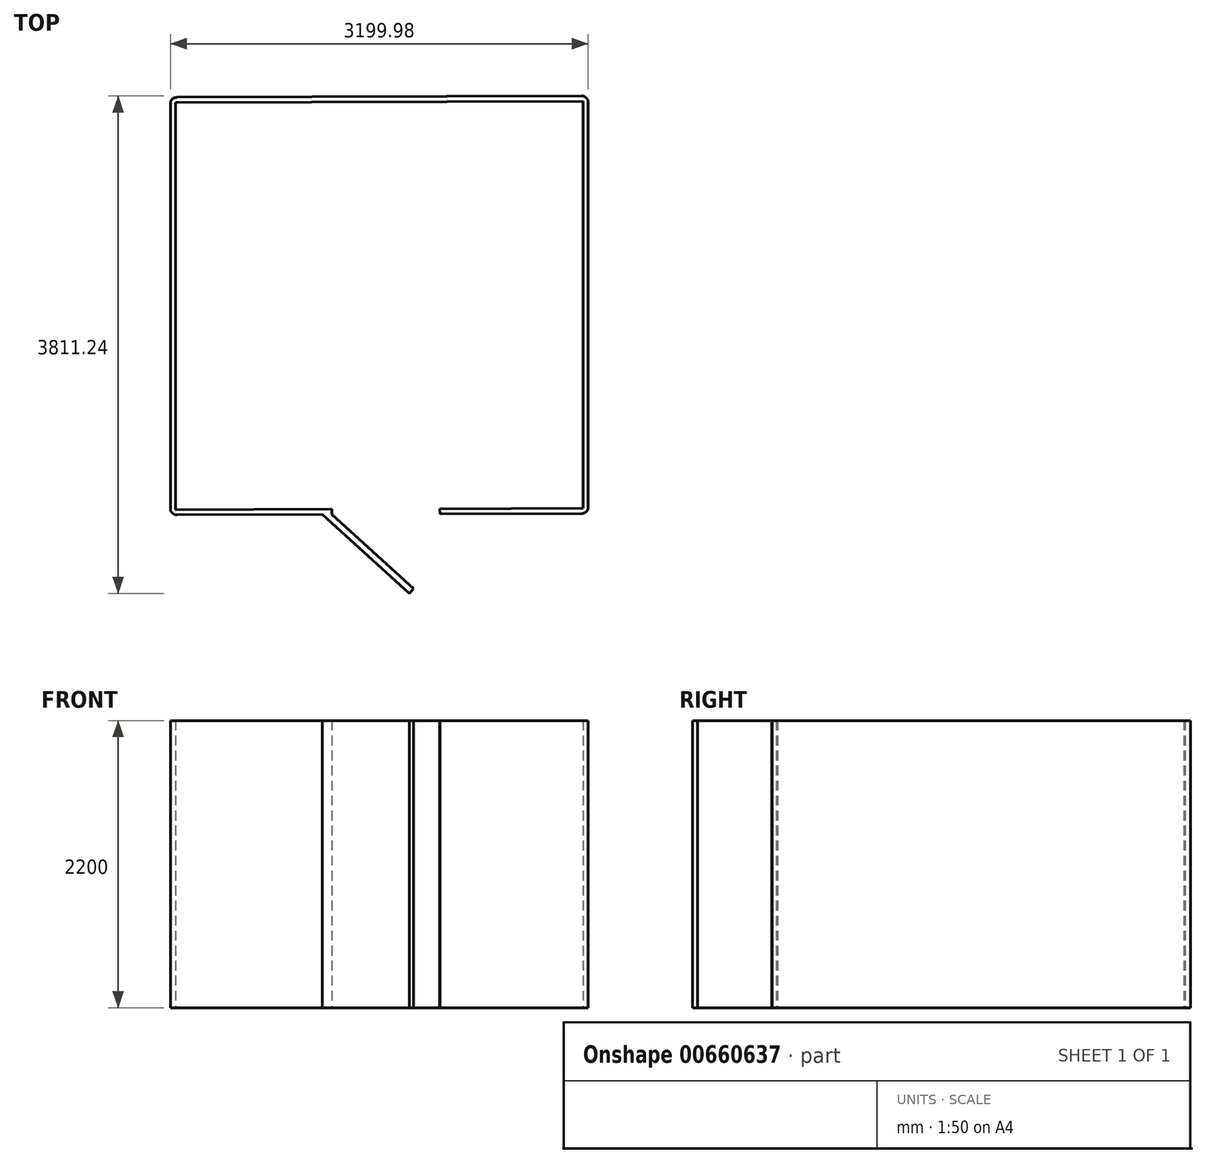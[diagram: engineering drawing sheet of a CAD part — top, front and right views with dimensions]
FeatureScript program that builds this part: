
annotation { "Feature Type Name" : "Feature", "Feature Type Description" : "" }
export const myFeature = defineFeature(function(context is Context, id is Id, definition is map)
    precondition{}
    {
        {
            var Q0;
            Q0=qCreatedBy(makeId("Top.planeOp"),FACE);
            var sketch = newSketch(context, id + "F0", { "sketchPlane" : qUnion([Q0])});
            skLineSegment(sketch, "E0", {"start": v(-163.84, 2276.46) * mm, "end": v(-163.84, -823.54) * mm});
            skLineSegment(sketch, "E1", {"start": v(-113.68, -873.54) * mm, "end": v(998.4, -869.87) * mm});
            skLineSegment(sketch, "E2", {"start": v(3036.14, -813.3) * mm, "end": v(3036.14, 2286.7) * mm});
            skLineSegment(sketch, "E3", {"start": v(2985.98, 2336.7) * mm, "end": v(-114, 2326.46) * mm});
            skLineSegment(sketch, "E4.0", {"start": v(-123.84, 2286.42) * mm, "end": v(-123.84, -833.58) * mm});
            skLineSegment(sketch, "E4.1", {"start": v(2996.14, 2296.74) * mm, "end": v(-123.84, 2286.42) * mm});
            skLineSegment(sketch, "E4.2", {"start": v(2996.14, -823.26) * mm, "end": v(2996.14, 2296.74) * mm});
            skLineSegment(sketch, "E4.3", {"start": v(-123.84, -833.58) * mm, "end": v(1072.4, -829.62) * mm});
            skPoint(sketch, "E5.visualSharp", {"position": v(-163.84, 2326.3) * mm});
            skArc(sketch, "E5.filletArc", {"start": v(-114, 2326.46) * mm, "mid": v(-149.25, 2311.75) * mm, "end": v(-163.84, 2276.46) * mm});
            skPoint(sketch, "E6.visualSharp", {"position": v(-163.84, -873.7) * mm});
            skArc(sketch, "E6.filletArc", {"start": v(-163.84, -823.54) * mm, "mid": v(-149.14, -858.96) * mm, "end": v(-113.68, -873.54) * mm});
            skPoint(sketch, "E7.visualSharp", {"position": v(3036.14, -863.13) * mm});
            skArc(sketch, "E7.filletArc", {"start": v(2986.3, -863.3) * mm, "mid": v(3021.56, -848.6) * mm, "end": v(3036.14, -813.3) * mm});
            skPoint(sketch, "E8.visualSharp", {"position": v(3036.14, 2336.87) * mm});
            skArc(sketch, "E8.filletArc", {"start": v(3036.14, 2286.7) * mm, "mid": v(3021.44, 2322.12) * mm, "end": v(2985.98, 2336.7) * mm});
            skLineSegment(sketch, "E9", {"start": v(998.4, -869.87) * mm, "end": v(1665, -1474.54) * mm});
            skLineSegment(sketch, "E10", {"start": v(1665, -1474.54) * mm, "end": v(1698.6, -1437.5) * mm});
            skLineSegment(sketch, "E11", {"start": v(1698.6, -1437.5) * mm, "end": v(1072.54, -869.62) * mm});
            skLineSegment(sketch, "E12", {"start": v(1072.54, -869.62) * mm, "end": v(1072.4, -829.62) * mm});
            skLineSegment(sketch, "E13", {"start": v(1900.83, -866.88) * mm, "end": v(1899.57, -826.89) * mm});
            skLineSegment(sketch, "E14.trimOffspring", {"start": v(1900.83, -866.88) * mm, "end": v(2986.3, -863.3) * mm});
            skLineSegment(sketch, "E15.trimOffspring", {"start": v(1899.57, -826.89) * mm, "end": v(2996.14, -823.26) * mm});
            skSolve(sketch);
        }
        {
            var Q0;
            Q0=makeQuery(id+"F0.imprint","IMPRINT",FACE,{"disambiguationData":[TD([[makeQuery(id+"F0.imprint","IMPRINT",EDGE,{"derivedFrom":sQuery(id+"F0.wireOp",EDGE,"E0")}),1.0]])]});
            extrude(context, id + "F1", {"entities" : qUnion([Q0]), "depth" : 2200 * mm, "offsetDistance" : 25 * mm});
        }
    });
